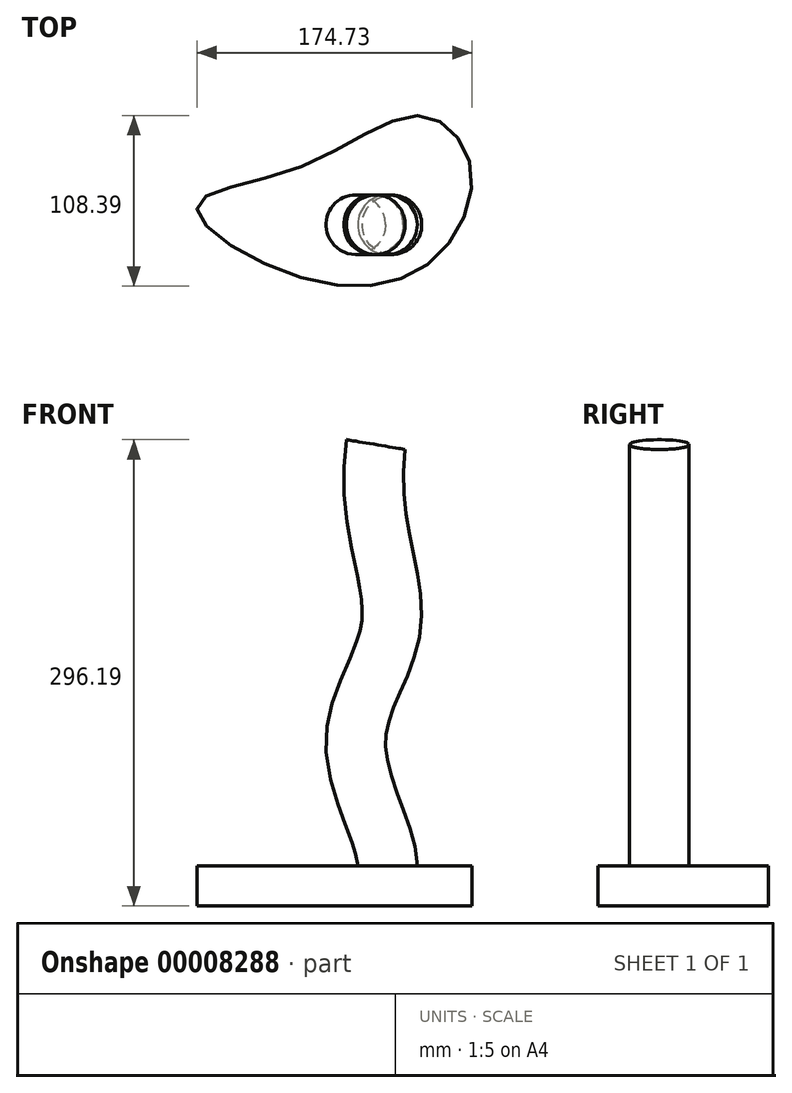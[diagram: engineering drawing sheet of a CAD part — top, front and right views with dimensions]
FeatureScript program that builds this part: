
annotation { "Feature Type Name" : "Feature", "Feature Type Description" : "" }
export const myFeature = defineFeature(function(context is Context, id is Id, definition is map)
    precondition{}
    {
        {
            var Q0;
            Q0=qCreatedBy(makeId("Top.planeOp"),FACE);
            var sketch = newSketch(context, id + "F0", { "sketchPlane" : qUnion([Q0])});
            skFitSpline(sketch, "E0", {"points": [v(-47.23, 25.52) * mm, v(28.45, 57.79) * mm, v(60.43, 24.93) * mm, v(33.44, -36.37) * mm, v(-51.63, -43.7) * mm, v(-113.52, 0) * mm, v(-47.23, 25.52) * mm]});
            skSolve(sketch);
        }
        {
            var Q0;
            Q0=makeQuery(id+"F0.imprint","IMPRINT",FACE,{"disambiguationData":[TD([[makeQuery(id+"F0.imprint","IMPRINT",EDGE,{"derivedFrom":sQuery(id+"F0.wireOp",EDGE,"E0")}),-1.0]])]});
            extrude(context, id + "F1", {"entities" : qUnion([Q0]), "depth" : 25.4 * mm});
        }
        {
            var Q0;
            Q0=qCreatedBy(makeId("Top.planeOp"),FACE);
            var sketch = newSketch(context, id + "F2", { "sketchPlane" : qUnion([Q0])});
            skCircle(sketch, "E1", {"center": v(-148.3, 84.3) * mm, "radius": 38.36 * mm});
            skSolve(sketch);
        }
        {
            var Q0;
            Q0=makeQuery(id+"F2.imprint","IMPRINT",FACE,{"disambiguationData":[TD([[makeQuery(id+"F2.imprint","IMPRINT",EDGE,{"derivedFrom":sQuery(id+"F2.wireOp",EDGE,"E1")}),1.0]])]});
            extrude(context, id + "F3", {"entities" : qUnion([Q0]), "depth" : 25.4 * mm});
        }
        {
            var Q0;
            Q0=makeQuery(id+"F3.opExtrude","SWEPT_BODY",BODY,{"disambiguationData":[OSD([sQuery(id+"F2.wireOp",EDGE,"E1")])]});
            deleteBodies(context, id + "F4", {"entities" : qUnion([Q0])});
        }
        {
            var Q0;
            Q0=makeQuery(id+"F1.opExtrude","CAP_FACE",FACE,{"disambiguationData":[OSD([sQuery(id+"F0.wireOp",EDGE,"E0")])],"isStart":false});
            var sketch = newSketch(context, id + "F5", { "sketchPlane" : qUnion([Q0])});
            skCircle(sketch, "E2", {"center": v(7.5, -11.46) * mm, "radius": 18.9 * mm});
            skSolve(sketch);
        }
        {
            var Q0;
            Q0=qCreatedBy(makeId("Front.planeOp"),FACE);
            var Q1;
            Q1=sQuery(id+"F5.wireOp",VERTEX,"E2.center");
            cPlane(context, id + "F6", {"entities" : qUnion([Q0, Q1]), "cplaneType" : CPlaneType.PLANE_POINT, "offset" : 152.4 * mm, "width" : 152.4 * mm, "height" : 152.4 * mm});
        }
        {
            var Q0;
            Q0=qCreatedBy(id+"F6.planeOp",FACE);
            var sketch = newSketch(context, id + "F7", { "sketchPlane" : qUnion([Q0])});
            skFitSpline(sketch, "E3", {"points": [v(7.5, 25.4) * mm, v(-12.77, 103.85) * mm, v(9.83, 178.3) * mm, v(0, 293.07) * mm], "startDerivative": vector(-4.37, 183.6) * mm, "endDerivative": vector(55.82, 390.76) * mm});
            skSolve(sketch);
        }
        {
            var Q0;
            Q0 = qSketchRegion(id + "F5", true);
            var Q1;
            Q1 = qBodyType(qCreatedBy(id + "F7" ,EDGE), BodyType.WIRE);
            sweep(context, id + "F8", {"profiles" : qUnion([Q0]), "path" : qUnion([Q1])});
        }
    });
